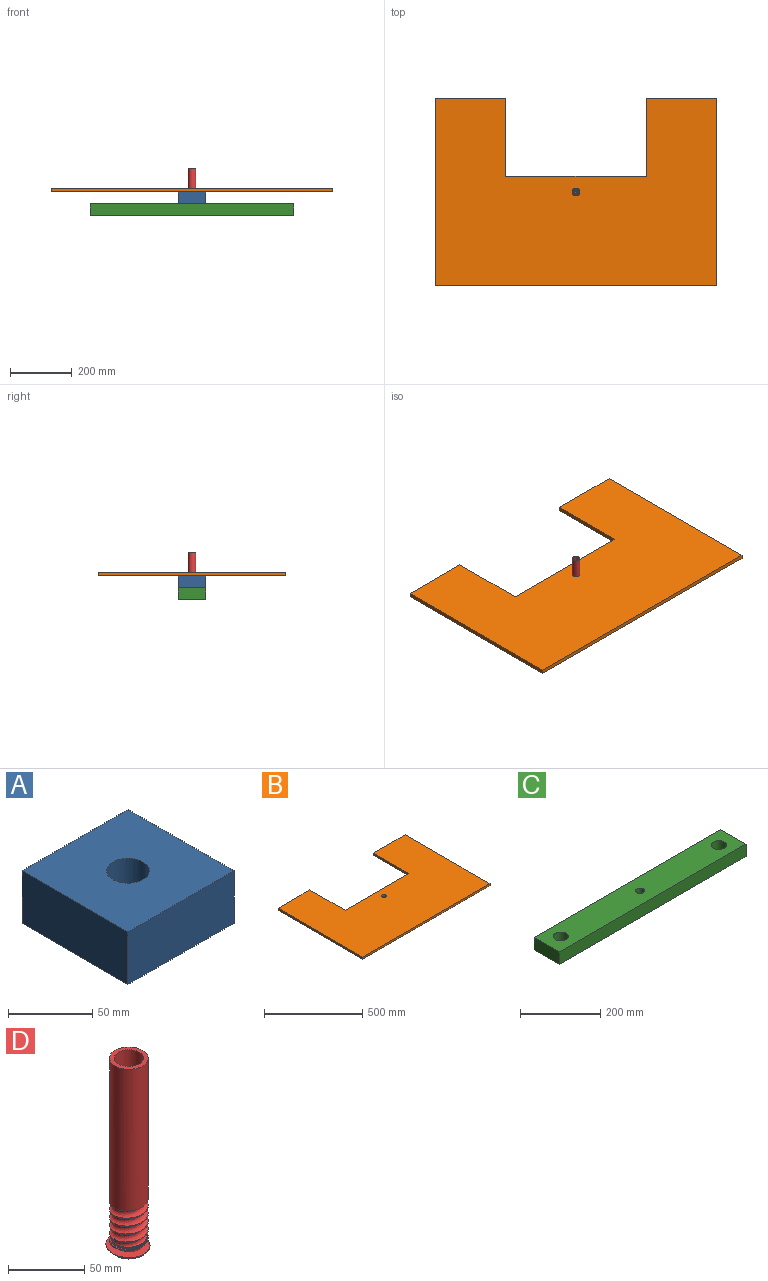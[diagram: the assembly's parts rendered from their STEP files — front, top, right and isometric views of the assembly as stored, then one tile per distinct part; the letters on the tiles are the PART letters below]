
ASSEMBLY  parts=4 mates=3
PART A: 7 faces, bbox 88.9x88.9x38.1 mm
  f0: plane 88.9x38.1mm, normal (0,1,0), area 3387.1mm2, adj f1,f3,f4,f5
  f1: plane 88.9x88.9mm, normal (0,0,1), area 7396.5mm2, adj f0,f2,f4,f5,f6
  f2: plane 88.9x38.1mm, normal (0,-1,0), area 3387.1mm2, adj f1,f3,f4,f5
  f3: plane 88.9x88.9mm, normal (0,0,-1), area 7396.5mm2, adj f0,f2,f4,f5,f6
  f4: plane 88.9x38.1mm, normal (1,0,0), area 3387.1mm2, adj f0,f1,f2,f3
  f5: plane 88.9x38.1mm, normal (-1,0,0), area 3387.1mm2, adj f0,f1,f2,f3
  f6: cylinder r=12.7mm len=38.1mm, axis (0,0,1), area 3040.2mm2, adj f1,f3
PART B: 11 faces, bbox 914.4x609.6x12.7 mm
  f0: plane 914.4x12.7mm, normal (0,-1,0), area 11612.9mm2, adj f1,f7,f9,f10
  f1: plane 609.6x12.7mm, normal (1,0,0), area 7741.9mm2, adj f0,f2,f9,f10
  f2: plane 228.6x12.7mm, normal (0,1,0), area 2903.2mm2, adj f1,f3,f9,f10
  f3: plane 254x12.7mm, normal (-1,0,0), area 3225.8mm2, adj f2,f4,f9,f10
  f4: plane 457.2x12.7mm, normal (0,1,0), area 5806.4mm2, adj f3,f5,f9,f10
  f5: plane 254x12.7mm, normal (1,0,0), area 3225.8mm2, adj f4,f6,f9,f10
  f6: plane 228.6x12.7mm, normal (0,1,0), area 2903.2mm2, adj f5,f7,f9,f10
  f7: plane 609.6x12.7mm, normal (-1,0,0), area 7741.9mm2, adj f0,f6,f9,f10
  f8: cylinder r=12.7mm len=25.4mm, axis (0,0,-1), area 1013.4mm2, adj f9,f10
  f9: plane 914.4x609.6mm, normal (0,0,1), area 440782.7mm2, adj f0,f1,f2,f3,f4,f5,f6,f7
  f10: plane 914.4x609.6mm, normal (0,0,-1), area 440782.7mm2, adj f0,f1,f2,f3,f4,f5,f6,f7
PART C: 9 faces, bbox 660.4x88.9x38.1 mm
  f0: plane 660.4x38.1mm, normal (0,1,0), area 25161.2mm2, adj f1,f3,f4,f5
  f1: plane 660.4x88.9mm, normal (0,0,1), area 56041.4mm2, adj f0,f2,f4,f5,f6,f7,f8
  f2: plane 660.4x38.1mm, normal (0,-1,0), area 25161.2mm2, adj f1,f3,f4,f5
  f3: plane 660.4x88.9mm, normal (0,0,-1), area 56041.4mm2, adj f0,f2,f4,f5,f6,f7,f8
  f4: plane 88.9x38.1mm, normal (1,0,0), area 3387.1mm2, adj f0,f1,f2,f3
  f5: plane 88.9x38.1mm, normal (-1,0,0), area 3387.1mm2, adj f0,f1,f2,f3
  f6: cylinder r=11.11mm len=38.1mm, axis (0,0,1), area 2660.2mm2, adj f1,f3
  f7: cylinder r=19.05mm len=38.1mm, axis (0,0,1), area 4560.4mm2, adj f1,f3
  f8: cylinder r=19.05mm len=38.1mm, axis (0,0,1), area 4560.4mm2, adj f1,f3
PART D: 15 faces, bbox 37.6x43.3x156 mm
  f0: cylinder r=9.53mm len=152.4mm, axis (0,0,-1), area 9120.7mm2, adj f1,f2
  f1: plane 25.4x25.4mm, normal (0,0,1), area 221.7mm2, adj f0,f3
  f2: plane 25.4x23.08mm, normal (0,0,-1), area 149.6mm2, adj f0,f4,f5,f6
  f3: cylinder r=12.7mm len=117.81mm, axis (0,0,-1), area 9147.5mm2, adj f1,f7,f8,f9
  f4: bspline ~29.33x25.4mm, area 230.2mm2, adj f2,f5,f6,f10
  f5: plane 3.65x3.65mm, normal (0,1,0), area 6.3mm2, adj f2,f4,f6
  f6: cylinder r=12.7mm len=25.4mm, axis (0,0,-1), area 77.5mm2, adj f2,f4,f5,f10
  f7: plane 6.49x3.65mm, normal (0,-1,0), area 12.7mm2, adj f3,f9
  f8: cylinder r=12.7mm len=25.4mm, axis (0,0,-1), area 53.3mm2, adj f3,f9,f11
  f9: bspline ~40.61x29.33mm, area 3064.5mm2, adj f3,f7,f8,f10,f11,f12,f13
  f10: cylinder r=12.7mm len=25.4mm, axis (0,0,-1), area 5.4mm2, adj f4,f6,f9,f12,f14
  f11: cylinder r=12.7mm len=25.4mm, axis (0,0,-1), area 53.4mm2, adj f8,f9,f13
  f12: cylinder r=12.7mm len=25.4mm, axis (0,0,-1), area 53mm2, adj f9,f10,f13
  f13: cylinder r=12.7mm len=25.4mm, axis (0,0,-1), area 53.4mm2, adj f9,f11,f12
  f14: bspline ~42.45x36.76mm, area 18.7mm2, adj f10
PLACE A t=(-44.45,0,19.05)mm
PLACE B t=(0,0,38.1)mm
PLACE C t=(-330.2,0,-19.05)mm
PLACE D t=(0,0,-38.1)mm
MATE fastened C.f6 <-> D.f0  axis (0,0,-1) through (0,0,-38.1)mm
MATE revolute B.f8 <-> D.f3  axis (0,0,1) through (0,0,50.8)mm
MATE fastened A.f6 <-> C.f6  axis (0,0,-1) through (0,0,0)mm
